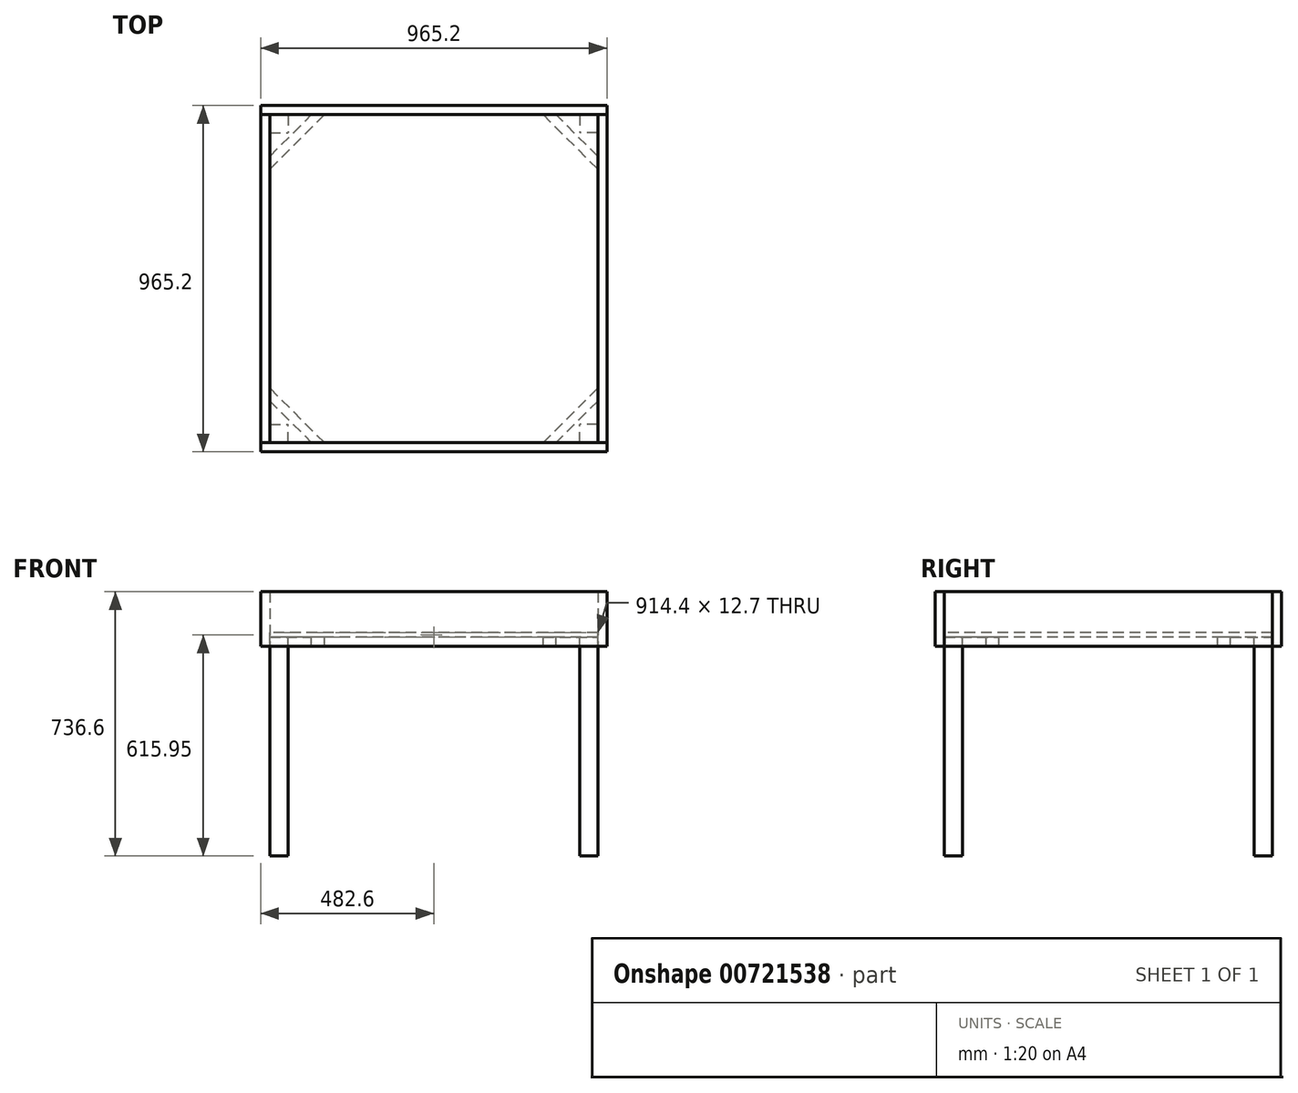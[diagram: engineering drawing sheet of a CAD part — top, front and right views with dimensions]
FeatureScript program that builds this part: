
annotation { "Feature Type Name" : "Feature", "Feature Type Description" : "" }
export const myFeature = defineFeature(function(context is Context, id is Id, definition is map)
    precondition{}
    {
        {
            var Q0;
            Q0=qCreatedBy(makeId("Top.planeOp"),FACE);
            var sketch = newSketch(context, id + "F0", { "sketchPlane" : qUnion([Q0])});
            skLineSegment(sketch, "E0.bottom", {"start": v(457.2, 457.2) * mm, "end": v(-457.2, 457.2) * mm});
            skLineSegment(sketch, "E0.top", {"start": v(457.2, -457.2) * mm, "end": v(-457.2, -457.2) * mm});
            skLineSegment(sketch, "E0.left", {"start": v(457.2, 457.2) * mm, "end": v(457.2, -457.2) * mm});
            skLineSegment(sketch, "E0.right", {"start": v(-457.2, 457.2) * mm, "end": v(-457.2, -457.2) * mm});
            skPoint(sketch, "E0.middle", {"position": v(0, 0) * mm});
            skSolve(sketch);
        }
        {
            var Q0;
            Q0 = qSketchRegion(id + "F0", true);
            extrude(context, id + "F1", {"entities" : qUnion([Q0]), "oppositeDirection" : true, "depth" : 12.7 * mm, "offsetDistance" : 25.4 * mm});
        }
        {
            var Q0;
            Q0=makeQuery(id+"F1.opExtrude","SWEPT_FACE",FACE,{"disambiguationData":[OSD([sQuery(id+"F0.wireOp",EDGE,"E0.bottom")])]});
            var sketch = newSketch(context, id + "F2", { "sketchPlane" : qUnion([Q0])});
            skLineSegment(sketch, "E1.bottom", {"start": v(-482.6, 114.3) * mm, "end": v(482.6, 114.3) * mm});
            skLineSegment(sketch, "E1.top", {"start": v(-482.6, -38.1) * mm, "end": v(482.6, -38.1) * mm});
            skLineSegment(sketch, "E1.left", {"start": v(-482.6, 114.3) * mm, "end": v(-482.6, -38.1) * mm});
            skLineSegment(sketch, "E1.right", {"start": v(482.6, 114.3) * mm, "end": v(482.6, -38.1) * mm});
            skSolve(sketch);
        }
        {
            var Q0;
            Q0 = qSketchRegion(id + "F2", true);
            extrude(context, id + "F3", {"entities" : qUnion([Q0]), "operationType" : NewBodyOperationType.ADD, "depth" : 25.4 * mm, "offsetDistance" : 25.4 * mm});
        }
        {
            var Q0;
            Q0=makeQuery(id+"F1.opExtrude","SWEPT_FACE",FACE,{"disambiguationData":[OSD([sQuery(id+"F0.wireOp",EDGE,"E0.top")])]});
            var sketch = newSketch(context, id + "F4", { "sketchPlane" : qUnion([Q0])});
            skLineSegment(sketch, "E2.bottom", {"start": v(-482.6, 114.3) * mm, "end": v(482.6, 114.3) * mm});
            skLineSegment(sketch, "E2.top", {"start": v(-482.6, -38.1) * mm, "end": v(482.6, -38.1) * mm});
            skLineSegment(sketch, "E2.left", {"start": v(-482.6, 114.3) * mm, "end": v(-482.6, -38.1) * mm});
            skLineSegment(sketch, "E2.right", {"start": v(482.6, 114.3) * mm, "end": v(482.6, -38.1) * mm});
            skSolve(sketch);
        }
        {
            var Q0;
            Q0 = qSketchRegion(id + "F4", true);
            extrude(context, id + "F5", {"entities" : qUnion([Q0]), "operationType" : NewBodyOperationType.ADD, "depth" : 25.4 * mm, "offsetDistance" : 25.4 * mm});
        }
        {
            var Q0;
            Q0=makeQuery(id+"F1.opExtrude","SWEPT_FACE",FACE,{"disambiguationData":[OSD([sQuery(id+"F0.wireOp",EDGE,"E0.right")])]});
            var sketch = newSketch(context, id + "F6", { "sketchPlane" : qUnion([Q0])});
            skLineSegment(sketch, "E3.bottom", {"start": v(-457.2, 114.3) * mm, "end": v(457.2, 114.3) * mm});
            skLineSegment(sketch, "E3.top", {"start": v(-457.2, -38.1) * mm, "end": v(457.2, -38.1) * mm});
            skLineSegment(sketch, "E3.left", {"start": v(-457.2, 114.3) * mm, "end": v(-457.2, -38.1) * mm});
            skLineSegment(sketch, "E3.right", {"start": v(457.2, 114.3) * mm, "end": v(457.2, -38.1) * mm});
            skSolve(sketch);
        }
        {
            var Q0;
            Q0 = qSketchRegion(id + "F6", true);
            extrude(context, id + "F7", {"entities" : qUnion([Q0]), "depth" : 25.4 * mm, "offsetDistance" : 25.4 * mm});
        }
        {
            var Q0;
            Q0=makeQuery(id+"F1.opExtrude","SWEPT_FACE",FACE,{"disambiguationData":[OSD([sQuery(id+"F0.wireOp",EDGE,"E0.left")])]});
            var sketch = newSketch(context, id + "F8", { "sketchPlane" : qUnion([Q0])});
            skLineSegment(sketch, "E4.bottom", {"start": v(457.2, 114.3) * mm, "end": v(-457.2, 114.3) * mm});
            skLineSegment(sketch, "E4.top", {"start": v(457.2, -38.1) * mm, "end": v(-457.2, -38.1) * mm});
            skLineSegment(sketch, "E4.left", {"start": v(457.2, 114.3) * mm, "end": v(457.2, -38.1) * mm});
            skLineSegment(sketch, "E4.right", {"start": v(-457.2, 114.3) * mm, "end": v(-457.2, -38.1) * mm});
            skSolve(sketch);
        }
        {
            var Q0;
            Q0 = qSketchRegion(id + "F8", true);
            extrude(context, id + "F9", {"entities" : qUnion([Q0]), "depth" : 25.4 * mm, "offsetDistance" : 25.4 * mm});
        }
        {
            var Q0;
            Q0=makeQuery(id+"F1.opExtrude","CAP_FACE",FACE,{"disambiguationData":[OSD([sQuery(id+"F0.wireOp",EDGE,"E0.bottom"),sQuery(id+"F0.wireOp",EDGE,"E0.top"),sQuery(id+"F0.wireOp",EDGE,"E0.left"),sQuery(id+"F0.wireOp",EDGE,"E0.right")])],"isStart":false});
            var sketch = newSketch(context, id + "F10", { "sketchPlane" : qUnion([Q0])});
            skLineSegment(sketch, "E5", {"start": v(-304.8, 457.2) * mm, "end": v(-457.2, 304.8) * mm});
            skLineSegment(sketch, "E6", {"start": v(-457.2, 340.72) * mm, "end": v(-340.72, 457.2) * mm});
            skLineSegment(sketch, "E7.MirrorCS", {"start": v(304.8, 457.2) * mm, "end": v(457.2, 304.8) * mm});
            skLineSegment(sketch, "E8.MirrorCS", {"start": v(457.2, 340.72) * mm, "end": v(340.72, 457.2) * mm});
            skLineSegment(sketch, "E9.MirrorCS", {"start": v(457.2, -340.72) * mm, "end": v(340.72, -457.2) * mm});
            skLineSegment(sketch, "E10.MirrorCS", {"start": v(304.8, -457.2) * mm, "end": v(457.2, -304.8) * mm});
            skLineSegment(sketch, "E11.MirrorCS", {"start": v(-304.8, -457.2) * mm, "end": v(-457.2, -304.8) * mm});
            skLineSegment(sketch, "E12.MirrorCS", {"start": v(-457.2, -340.72) * mm, "end": v(-340.72, -457.2) * mm});
            skLineSegment(sketch, "E13", {"start": v(-340.72, 457.2) * mm, "end": v(-304.8, 457.2) * mm});
            skLineSegment(sketch, "E14", {"start": v(-457.2, 340.72) * mm, "end": v(-457.2, 304.8) * mm});
            skLineSegment(sketch, "E15", {"start": v(304.8, 457.2) * mm, "end": v(340.72, 457.2) * mm});
            skLineSegment(sketch, "E16", {"start": v(457.2, 340.72) * mm, "end": v(457.2, 304.8) * mm});
            skLineSegment(sketch, "E17", {"start": v(-457.2, -304.8) * mm, "end": v(-457.2, -340.72) * mm});
            skLineSegment(sketch, "E18", {"start": v(-340.72, -457.2) * mm, "end": v(-304.8, -457.2) * mm});
            skLineSegment(sketch, "E19", {"start": v(304.8, -457.2) * mm, "end": v(340.72, -457.2) * mm});
            skLineSegment(sketch, "E20", {"start": v(457.2, -304.8) * mm, "end": v(457.2, -340.72) * mm});
            skSolve(sketch);
        }
        {
            var Q0;
            Q0 = qSketchRegion(id + "F10", true);
            extrude(context, id + "F11", {"entities" : qUnion([Q0]), "depth" : 25.4 * mm, "offsetDistance" : 25.4 * mm});
        }
        {
            var Q0;
            Q0=makeQuery(id+"F1.opExtrude","CAP_FACE",FACE,{"disambiguationData":[OSD([sQuery(id+"F0.wireOp",EDGE,"E0.bottom"),sQuery(id+"F0.wireOp",EDGE,"E0.top"),sQuery(id+"F0.wireOp",EDGE,"E0.left"),sQuery(id+"F0.wireOp",EDGE,"E0.right")])],"isStart":false});
            var sketch = newSketch(context, id + "F12", { "sketchPlane" : qUnion([Q0])});
            skLineSegment(sketch, "E21.bottom", {"start": v(-457.2, 457.2) * mm, "end": v(-406.4, 457.2) * mm});
            skLineSegment(sketch, "E21.top", {"start": v(-457.2, 406.4) * mm, "end": v(-406.4, 406.4) * mm});
            skLineSegment(sketch, "E21.left", {"start": v(-457.2, 457.2) * mm, "end": v(-457.2, 406.4) * mm});
            skLineSegment(sketch, "E21.right", {"start": v(-406.4, 457.2) * mm, "end": v(-406.4, 406.4) * mm});
            skLineSegment(sketch, "E22.MirrorCS", {"start": v(406.4, 457.2) * mm, "end": v(406.4, 406.4) * mm});
            skLineSegment(sketch, "E23.MirrorCS", {"start": v(457.2, 457.2) * mm, "end": v(457.2, 406.4) * mm});
            skLineSegment(sketch, "E24.MirrorCS", {"start": v(457.2, 406.4) * mm, "end": v(406.4, 406.4) * mm});
            skLineSegment(sketch, "E25.MirrorCS", {"start": v(457.2, 457.2) * mm, "end": v(406.4, 457.2) * mm});
            skLineSegment(sketch, "E26.MirrorCS", {"start": v(406.4, -457.2) * mm, "end": v(406.4, -406.4) * mm});
            skLineSegment(sketch, "E27.MirrorCS", {"start": v(457.2, -457.2) * mm, "end": v(457.2, -406.4) * mm});
            skLineSegment(sketch, "E28.MirrorCS", {"start": v(457.2, -406.4) * mm, "end": v(406.4, -406.4) * mm});
            skLineSegment(sketch, "E29.MirrorCS", {"start": v(457.2, -457.2) * mm, "end": v(406.4, -457.2) * mm});
            skLineSegment(sketch, "E30.MirrorCS", {"start": v(-457.2, -457.2) * mm, "end": v(-457.2, -406.4) * mm});
            skLineSegment(sketch, "E31.MirrorCS", {"start": v(-406.4, -457.2) * mm, "end": v(-406.4, -406.4) * mm});
            skLineSegment(sketch, "E32.MirrorCS", {"start": v(-457.2, -406.4) * mm, "end": v(-406.4, -406.4) * mm});
            skLineSegment(sketch, "E33.MirrorCS", {"start": v(-457.2, -457.2) * mm, "end": v(-406.4, -457.2) * mm});
            skSolve(sketch);
        }
        {
            var Q0;
            Q0 = qSketchRegion(id + "F12", true);
            extrude(context, id + "F13", {"entities" : qUnion([Q0]), "depth" : 609.6 * mm, "offsetDistance" : 25.4 * mm});
        }
    });
